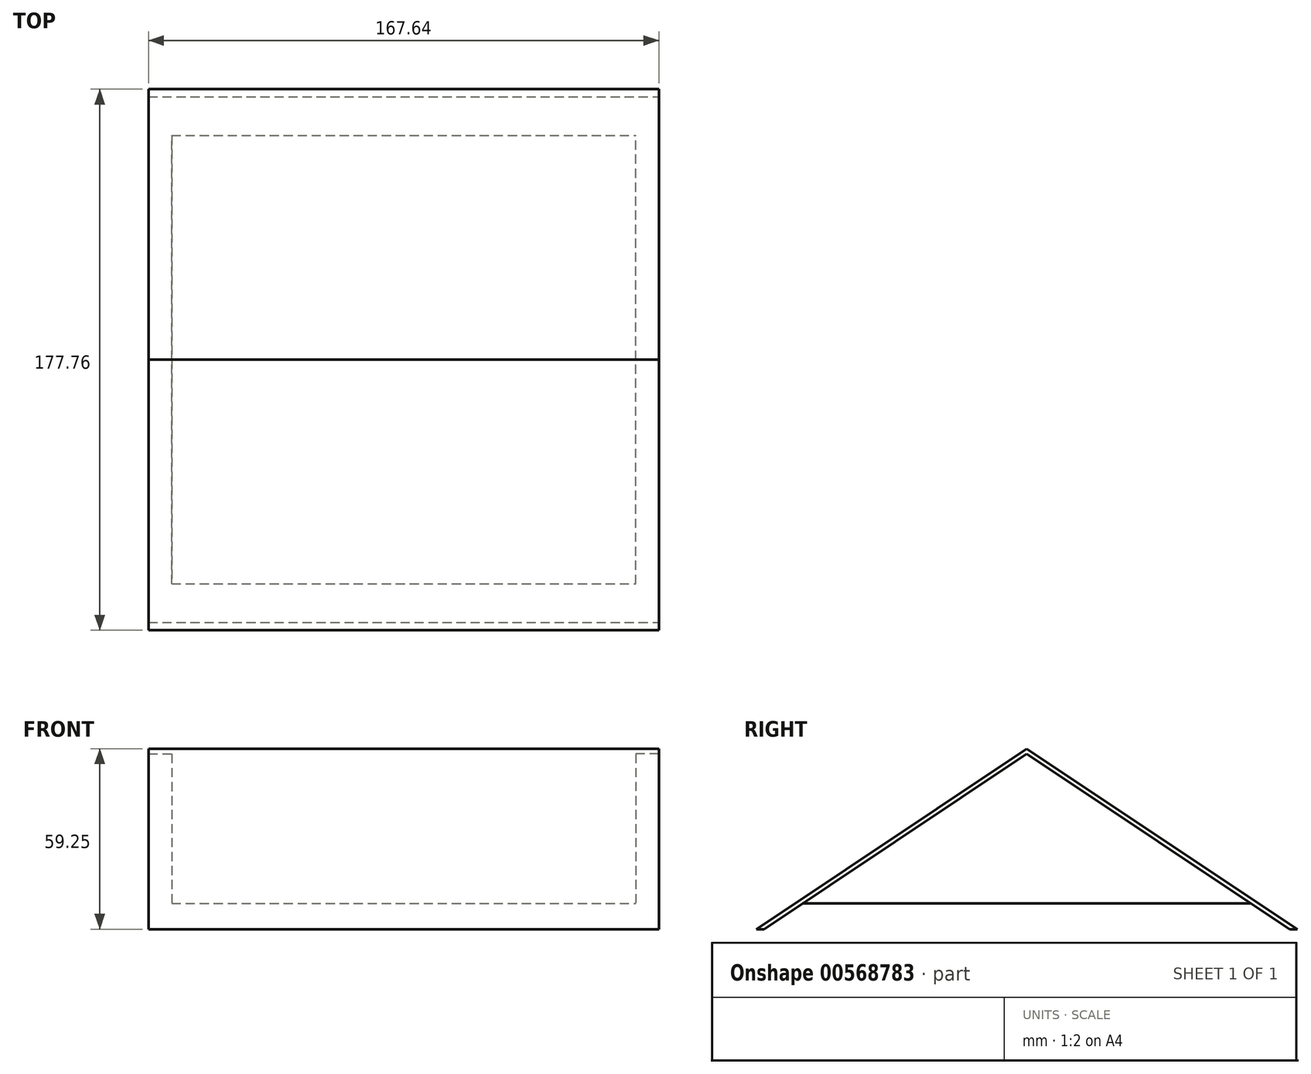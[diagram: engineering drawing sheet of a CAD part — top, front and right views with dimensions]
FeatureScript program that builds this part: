
annotation { "Feature Type Name" : "Feature", "Feature Type Description" : "" }
export const myFeature = defineFeature(function(context is Context, id is Id, definition is map)
    precondition{}
    {
        {
            var Q0;
            Q0=qCreatedBy(makeId("Top.planeOp"),FACE);
            var sketch = newSketch(context, id + "F0", { "sketchPlane" : qUnion([Q0])});
            skLineSegment(sketch, "E0.bottom", {"start": v(76.2, -76.2) * mm, "end": v(-76.2, -76.2) * mm});
            skLineSegment(sketch, "E0.top", {"start": v(76.2, 76.2) * mm, "end": v(-76.2, 76.2) * mm});
            skLineSegment(sketch, "E0.left", {"start": v(76.2, -76.2) * mm, "end": v(76.2, 76.2) * mm});
            skLineSegment(sketch, "E0.right", {"start": v(-76.2, -76.2) * mm, "end": v(-76.2, 76.2) * mm});
            skPoint(sketch, "E0.middle", {"position": v(0, 0) * mm});
            skSolve(sketch);
        }
        {
            var Q0;
            Q0 = qSketchRegion(id + "F0", true);
            extrude(context, id + "F1", {"entities" : qUnion([Q0]), "depth" : 50.8 * mm, "offsetDistance" : 25.4 * mm});
        }
        {
            var Q0;
            Q0=makeQuery(id+"F1.opExtrude","SWEPT_FACE",FACE,{"disambiguationData":[OSD([sQuery(id+"F0.wireOp",EDGE,"E0.right")])]});
            var sketch = newSketch(context, id + "F2", { "sketchPlane" : qUnion([Q0])});
            skLineSegment(sketch, "E1", {"start": v(0, 0) * mm, "end": v(0, 50.8) * mm, "construction": true});
            skLineSegment(sketch, "E2", {"start": v(0, 50.8) * mm, "end": v(76.2, 0) * mm});
            skLineSegment(sketch, "E3", {"start": v(76.2, 0) * mm, "end": v(-76.2, 0) * mm});
            skLineSegment(sketch, "E4", {"start": v(-76.2, 0) * mm, "end": v(0, 50.8) * mm});
            skSolve(sketch);
        }
        {
            var Q0;
            {var subQ0=sQuery(id+"F2.wireOp",EDGE,"E2");Q0=makeQuery(id+"F2.imprint","IMPRINT",FACE,{"disambiguationData":[TD([[makeQuery(id+"F2.imprint","IMPRINT",EDGE,{"derivedFrom":subQ0}),1.0]])]});}
            var Q1;
            {var subQ0=sQuery(id+"F2.wireOp",EDGE,"E4");Q1=makeQuery(id+"F2.imprint","IMPRINT",FACE,{"disambiguationData":[TD([[makeQuery(id+"F2.imprint","IMPRINT",EDGE,{"derivedFrom":subQ0}),1.0]])]});}
            extrude(context, id + "F3", {"entities" : qUnion([Q0, Q1]), "operationType" : NewBodyOperationType.REMOVE, "endBound" : BoundingType.THROUGH_ALL, "oppositeDirection" : true, "depth" : 25.4 * mm, "offsetDistance" : 25.4 * mm});
        }
        {
            var Q0;
            Q0=makeQuery(id+"F1.opExtrude","SWEPT_FACE",FACE,{"disambiguationData":[OSD([sQuery(id+"F0.wireOp",EDGE,"E0.left")])]});
            var sketch = newSketch(context, id + "F4", { "sketchPlane" : qUnion([Q0])});
            skLineSegment(sketch, "E5", {"start": v(-73.66, 0) * mm, "end": v(0, 49.1) * mm});
            skLineSegment(sketch, "E6", {"start": v(0, 49.1) * mm, "end": v(73.66, 0) * mm});
            skLineSegment(sketch, "E7", {"start": v(73.66, 0) * mm, "end": v(76.2, 0) * mm});
            skLineSegment(sketch, "E8", {"start": v(-76.2, 0) * mm, "end": v(-73.66, 0) * mm});
            skSolve(sketch);
        }
        {
            var Q0;
            Q0=makeQuery(id+"F4.imprint","IMPRINT",FACE,{"disambiguationData":[TD([[makeQuery(id+"F4.imprint","IMPRINT",EDGE,{"derivedFrom":sQuery(id+"F4.wireOp",EDGE,"E5")}),1.0]])]});
            extrude(context, id + "F5", {"entities" : qUnion([Q0]), "operationType" : NewBodyOperationType.ADD, "depth" : 7.62 * mm, "offsetDistance" : 25.4 * mm});
        }
        {
            var Q0;
            Q0=makeQuery(id+"F1.opExtrude","SWEPT_FACE",FACE,{"disambiguationData":[OSD([sQuery(id+"F0.wireOp",EDGE,"E0.right")])]});
            var sketch = newSketch(context, id + "F6", { "sketchPlane" : qUnion([Q0])});
            skLineSegment(sketch, "E9", {"start": v(-73.66, 0) * mm, "end": v(0, 49.1) * mm});
            skLineSegment(sketch, "E10", {"start": v(0, 49.1) * mm, "end": v(73.66, 0) * mm});
            skLineSegment(sketch, "E11", {"start": v(73.66, 0) * mm, "end": v(76.2, 0) * mm});
            skLineSegment(sketch, "E12", {"start": v(-73.66, 0) * mm, "end": v(-76.2, 0) * mm});
            skSolve(sketch);
        }
        {
            var Q0;
            Q0=makeQuery(id+"F6.imprint","IMPRINT",FACE,{"disambiguationData":[TD([[makeQuery(id+"F6.imprint","IMPRINT",EDGE,{"derivedFrom":sQuery(id+"F6.wireOp",EDGE,"E9")}),1.0]])]});
            extrude(context, id + "F7", {"entities" : qUnion([Q0]), "operationType" : NewBodyOperationType.ADD, "depth" : 7.62 * mm, "offsetDistance" : 25.4 * mm});
        }
        {
            var Q0;
            Q0=makeQuery(id+"F5.opExtrude","CAP_FACE",FACE,{"disambiguationData":[OSD([sQuery(id+"F0.wireOp",EDGE,"E0.left"),sQuery(id+"F2.wireOp",EDGE,"E2"),sQuery(id+"F2.wireOp",EDGE,"E4"),sQuery(id+"F4.wireOp",EDGE,"E5"),sQuery(id+"F4.wireOp",EDGE,"E6"),sQuery(id+"F4.wireOp",EDGE,"E7"),sQuery(id+"F4.wireOp",EDGE,"E8")])],"isStart":false});
            var sketch = newSketch(context, id + "F8", { "sketchPlane" : qUnion([Q0])});
            skLineSegment(sketch, "E13", {"start": v(73.66, 0) * mm, "end": v(86.34, -8.45) * mm});
            skLineSegment(sketch, "E14", {"start": v(86.34, -8.45) * mm, "end": v(88.88, -8.45) * mm});
            skLineSegment(sketch, "E15", {"start": v(88.88, -8.45) * mm, "end": v(76.2, 0) * mm});
            skLineSegment(sketch, "E16", {"start": v(-76.2, 0) * mm, "end": v(-88.88, -8.45) * mm});
            skLineSegment(sketch, "E17", {"start": v(-88.88, -8.45) * mm, "end": v(-86.34, -8.45) * mm});
            skLineSegment(sketch, "E18", {"start": v(-86.34, -8.45) * mm, "end": v(-73.66, 0) * mm});
            skSolve(sketch);
        }
        {
            var Q0;
            Q0=makeQuery(id+"F8.imprint","IMPRINT",FACE,{"disambiguationData":[TD([[makeQuery(id+"F8.imprint","IMPRINT",EDGE,{"derivedFrom":sQuery(id+"F8.wireOp",EDGE,"E16")}),1.0]])]});
            var Q1;
            Q1=makeQuery(id+"F8.imprint","IMPRINT",FACE,{"disambiguationData":[TD([[makeQuery(id+"F8.imprint","IMPRINT",EDGE,{"derivedFrom":sQuery(id+"F8.wireOp",EDGE,"E13")}),1.0]])]});
            extrude(context, id + "F9", {"entities" : qUnion([Q0, Q1]), "operationType" : NewBodyOperationType.ADD, "oppositeDirection" : true, "depth" : 167.64 * mm, "offsetDistance" : 25.4 * mm});
        }
    });
